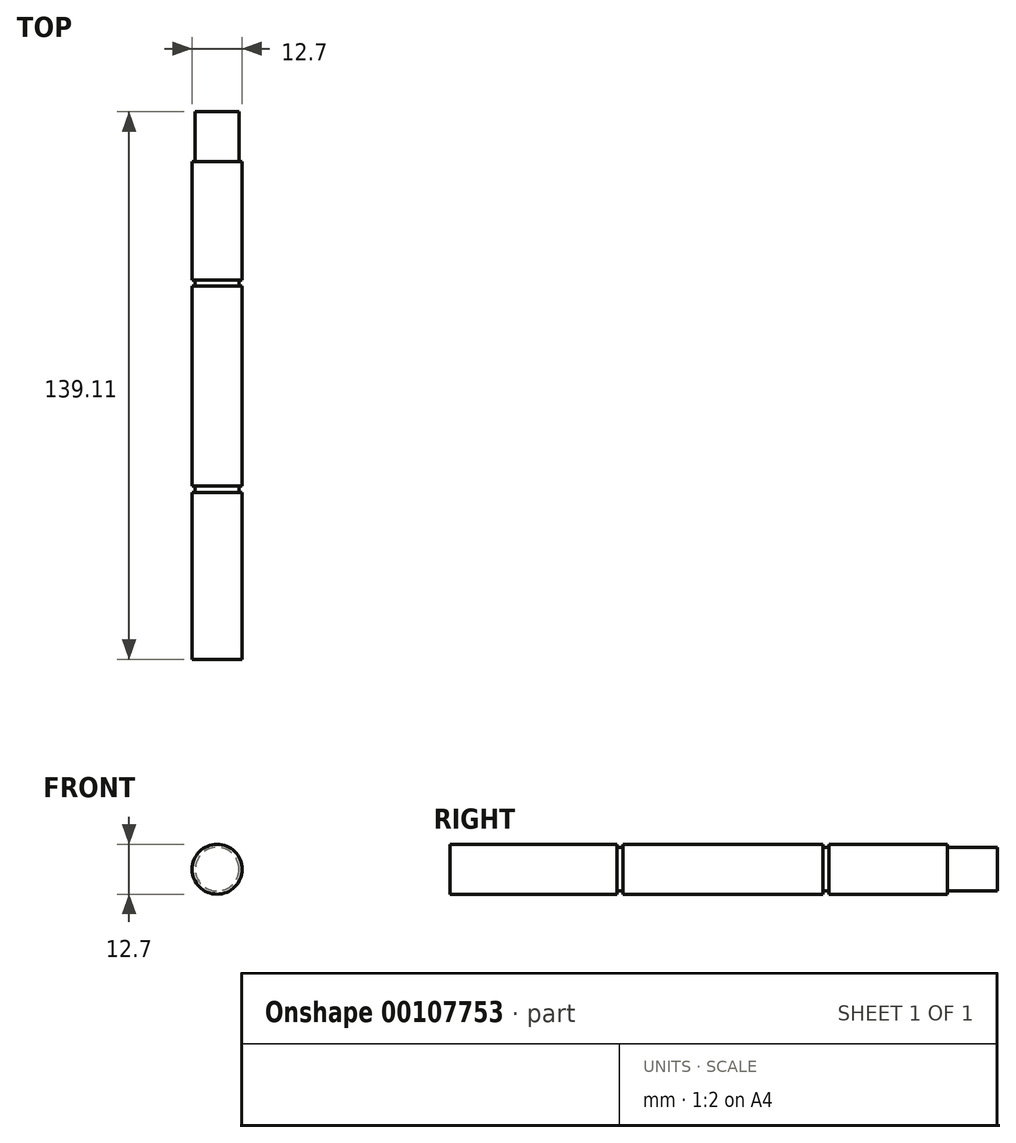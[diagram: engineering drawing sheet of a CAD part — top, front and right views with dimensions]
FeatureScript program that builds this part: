
annotation { "Feature Type Name" : "Feature", "Feature Type Description" : "" }
export const myFeature = defineFeature(function(context is Context, id is Id, definition is map)
    precondition{}
    {
        {
            var Q0;
            Q0=qCreatedBy(makeId("Front.planeOp"),FACE);
            var sketch = newSketch(context, id + "F0", { "sketchPlane" : qUnion([Q0])});
            skCircle(sketch, "E0", {"center": v(0, 0) * mm, "radius": 6.35 * mm});
            skSolve(sketch);
        }
        {
            var Q0;
            Q0 = qSketchRegion(id + "F0", true);
            extrude(context, id + "F1", {"entities" : qUnion([Q0]), "depth" : 42.42 * mm});
        }
        {
            var Q0;
            Q0=makeQuery(id+"F1.opExtrude","CAP_FACE",FACE,{"disambiguationData":[OSD([sQuery(id+"F0.wireOp",EDGE,"E0")])],"isStart":true});
            var sketch = newSketch(context, id + "F2", { "sketchPlane" : qUnion([Q0])});
            skCircle(sketch, "E1", {"center": v(0, 0) * mm, "radius": 5.56 * mm});
            skSolve(sketch);
        }
        {
            var Q0;
            Q0 = qSketchRegion(id + "F2", true);
            extrude(context, id + "F3", {"entities" : qUnion([Q0]), "operationType" : NewBodyOperationType.ADD, "depth" : 1.59 * mm});
        }
        {
            var Q0;
            Q0=makeQuery(id+"F3.opExtrude","CAP_FACE",FACE,{"disambiguationData":[OSD([sQuery(id+"F2.wireOp",EDGE,"E1")])],"isStart":false});
            var sketch = newSketch(context, id + "F4", { "sketchPlane" : qUnion([Q0])});
            skCircle(sketch, "E2", {"center": v(0, 0) * mm, "radius": 6.35 * mm});
            skSolve(sketch);
        }
        {
            var Q0;
            Q0 = qSketchRegion(id + "F4", true);
            extrude(context, id + "F5", {"entities" : qUnion([Q0]), "operationType" : NewBodyOperationType.ADD, "depth" : 50.8 * mm});
        }
        {
            var Q0;
            Q0=makeQuery(id+"F5.opExtrude","CAP_FACE",FACE,{"disambiguationData":[OSD([sQuery(id+"F4.wireOp",EDGE,"E2")])],"isStart":false});
            var sketch = newSketch(context, id + "F6", { "sketchPlane" : qUnion([Q0])});
            skCircle(sketch, "E3", {"center": v(0, 0) * mm, "radius": 5.56 * mm});
            skSolve(sketch);
        }
        {
            var Q0;
            Q0 = qSketchRegion(id + "F6", true);
            extrude(context, id + "F7", {"entities" : qUnion([Q0]), "operationType" : NewBodyOperationType.ADD, "depth" : 1.59 * mm});
        }
        {
            var Q0;
            Q0=makeQuery(id+"F7.opExtrude","CAP_FACE",FACE,{"disambiguationData":[OSD([sQuery(id+"F6.wireOp",EDGE,"E3")])],"isStart":false});
            var sketch = newSketch(context, id + "F8", { "sketchPlane" : qUnion([Q0])});
            skCircle(sketch, "E4", {"center": v(0, 0) * mm, "radius": 6.35 * mm});
            skSolve(sketch);
        }
        {
            var Q0;
            Q0 = qSketchRegion(id + "F8", true);
            extrude(context, id + "F9", {"entities" : qUnion([Q0]), "operationType" : NewBodyOperationType.ADD, "depth" : 30.01 * mm});
        }
        {
            var Q0;
            Q0=makeQuery(id+"F9.opExtrude","CAP_FACE",FACE,{"disambiguationData":[OSD([sQuery(id+"F8.wireOp",EDGE,"E4")])],"isStart":false});
            var sketch = newSketch(context, id + "F10", { "sketchPlane" : qUnion([Q0])});
            skCircle(sketch, "E5", {"center": v(0, 0) * mm, "radius": 5.56 * mm});
            skSolve(sketch);
        }
        {
            var Q0;
            Q0 = qSketchRegion(id + "F10", true);
            extrude(context, id + "F11", {"entities" : qUnion([Q0]), "operationType" : NewBodyOperationType.ADD, "depth" : 12.7 * mm});
        }
    });
